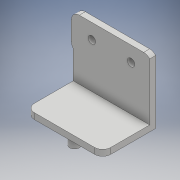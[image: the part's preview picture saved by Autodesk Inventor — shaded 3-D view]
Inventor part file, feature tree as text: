
AUTODESK INVENTOR PART (.ipt)
format: ipt  version: 2018 (Build 220112000, 112)  size: 150,016 bytes
history: native  units: mm
features: extrude x4, sketch x3, fillet x3
ambient origin geometry x8: Origin, YZ Plane, XZ Plane, XY Plane, X Axis, Y Axis, Z Axis, Center Point
bodies: Solid1 (feature_tree)
feature tree (10):
  extrude  "Extrusion1"  Depth=38.1mm
  sketch  "Sketch2"  dims[d2=19.558mm d5=1.0mm]
  extrude  "Extrusion2"  Depth=1.0mm
  extrude  "Extrusion3"  Depth=10.0mm
  fillet  "Fillet1"  Radius=3.0mm
  fillet  "Fillet2"  Radius=18.455mm
  fillet  "Fillet3"  Radius=3.0mm
  extrude  "Extrusion4"  Depth=10.0mm
  sketch  "Sketch1"  dims[d0=15.0mm d1=38.1mm]
  sketch  "Sketch3"  dims[d6=3.683mm d7=3.683mm d9=3.0mm d10=0.0mm d11=18.455mm d12=3.0mm d13=0.0mm d14=4.8mm d15=5.0mm d16=6.0mm d17=0.0mm d18=25.35mm d19=7.5mm d20=4.0mm d21=4.0mm d22=4.0mm d23=10.0mm d24=0.0mm]
